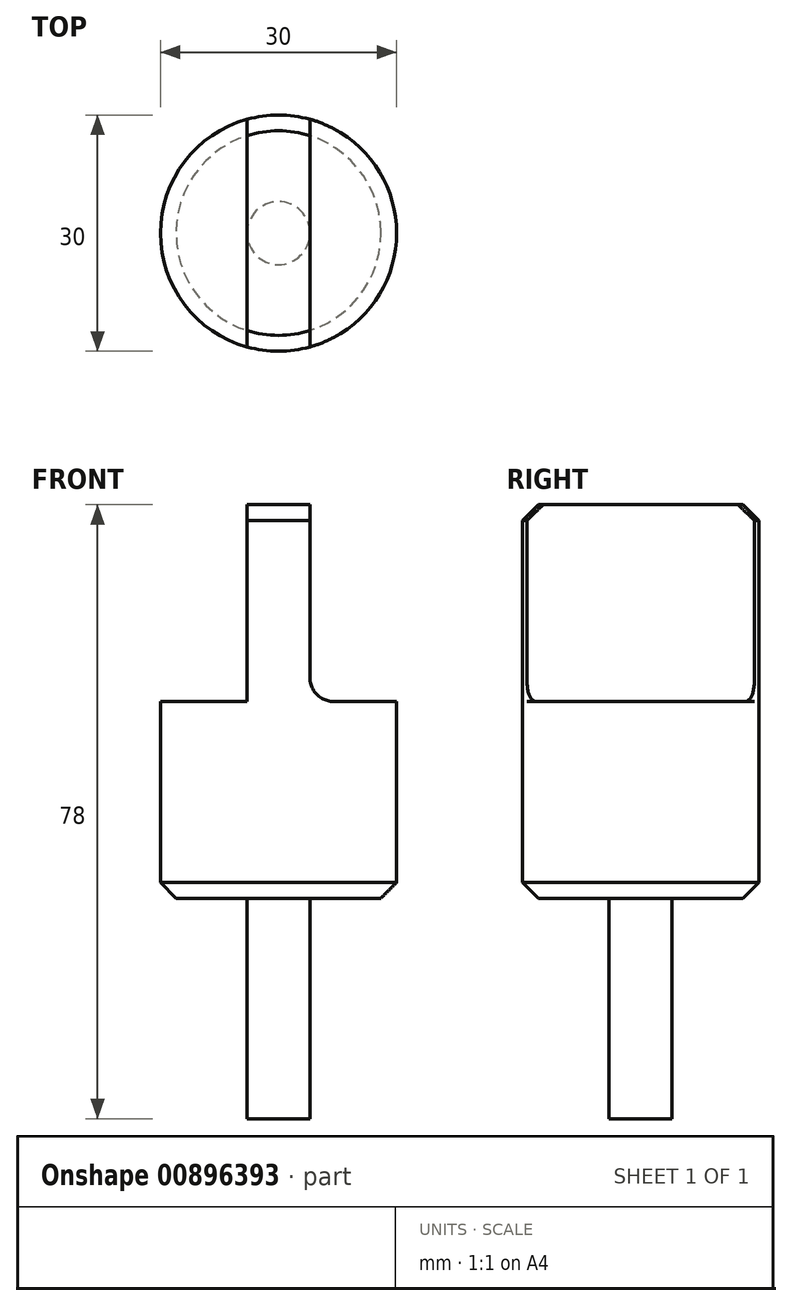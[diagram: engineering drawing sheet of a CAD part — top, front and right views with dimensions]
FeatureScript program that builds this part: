
annotation { "Feature Type Name" : "Feature", "Feature Type Description" : "" }
export const myFeature = defineFeature(function(context is Context, id is Id, definition is map)
    precondition{}
    {
        {
            var Q0;
            Q0=qCreatedBy(makeId("Top.planeOp"),FACE);
            var sketch = newSketch(context, id + "F0", { "sketchPlane" : qUnion([Q0])});
            skCircle(sketch, "E0", {"center": v(0, 0) * mm, "radius": 15 * mm});
            skCircle(sketch, "E1", {"center": v(0, 0) * mm, "radius": 4 * mm});
            skSolve(sketch);
        }
        {
            var Q0;
            Q0=makeQuery(id+"F0.imprint","IMPRINT",FACE,{"disambiguationData":[TD([[makeQuery(id+"F0.imprint","IMPRINT",EDGE,{"derivedFrom":sQuery(id+"F0.wireOp",EDGE,"E0")}),1.0]])]});
            var Q1;
            Q1=makeQuery(id+"F0.imprint","IMPRINT",FACE,{"disambiguationData":[TD([[makeQuery(id+"F0.imprint","IMPRINT",EDGE,{"derivedFrom":sQuery(id+"F0.wireOp",EDGE,"E1")}),1.0]])]});
            extrude(context, id + "F1", {"entities" : qUnion([Q0, Q1]), "depth" : 25 * mm, "offsetDistance" : 25 * mm});
        }
        {
            var Q0;
            Q0=makeQuery(id+"F0.imprint","IMPRINT",FACE,{"disambiguationData":[TD([[makeQuery(id+"F0.imprint","IMPRINT",EDGE,{"derivedFrom":sQuery(id+"F0.wireOp",EDGE,"E1")}),1.0]])]});
            extrude(context, id + "F2", {"entities" : qUnion([Q0]), "operationType" : NewBodyOperationType.ADD, "oppositeDirection" : true, "depth" : 28 * mm, "offsetDistance" : 25 * mm});
        }
        {
            var Q0;
            Q0=makeQuery(id+"F1.opExtrude","CAP_FACE",FACE,{"disambiguationData":[OSD([sQuery(id+"F0.wireOp",EDGE,"E0")])],"isStart":false});
            var sketch = newSketch(context, id + "F3", { "sketchPlane" : qUnion([Q0])});
            skLineSegment(sketch, "E2.left", {"start": v(4, 14.46) * mm, "end": v(4, -14.46) * mm});
            skLineSegment(sketch, "E2.right", {"start": v(-4, 14.46) * mm, "end": v(-4, -14.46) * mm});
            skPoint(sketch, "E2.middle", {"position": v(0, 0) * mm});
            skSolve(sketch);
        }
        {
            var Q0;
            {var subQ0=sQuery(id+"F3.wireOp",EDGE,"E2.left");Q0=makeQuery(id+"F3.imprint","IMPRINT",FACE,{"disambiguationData":[TD([[makeQuery(id+"F3.imprint","IMPRINT",EDGE,{"derivedFrom":subQ0}),-1.0]])]});}
            extrude(context, id + "F4", {"entities" : qUnion([Q0]), "operationType" : NewBodyOperationType.ADD, "depth" : 25 * mm, "offsetDistance" : 25 * mm});
        }
        {
            var Q0;
            {var subQ0=sQuery(id+"F0.wireOp",EDGE,"E0");var subQ1=makeQuery(id+"F1.opExtrude","CAP_EDGE",EDGE,{"disambiguationData":[OSD([subQ0])],"isStart":false});Q0=makeQuery(id+"F4.opExtrude","CAP_EDGE",EDGE,{"disambiguationData":[OSD([subQ0]),TDD([makeQuery(id+"F3.imprint","IMPRINT",EDGE,{"disambiguationData":[TD([[makeQuery(id+"F3.imprint","INTERSECT",VERTEX,{"disambiguationData":[OD(1.0)],"derivedFrom":[subQ1,sQuery(id+"F3.wireOp",EDGE,"E2.left")]}),1.0]])],"derivedFrom":subQ1})])],"isStart":false});}
            var Q1;
            {var subQ0=sQuery(id+"F0.wireOp",EDGE,"E0");var subQ1=makeQuery(id+"F1.opExtrude","CAP_EDGE",EDGE,{"disambiguationData":[OSD([subQ0])],"isStart":false});Q1=makeQuery(id+"F4.opExtrude","CAP_EDGE",EDGE,{"disambiguationData":[OSD([subQ0]),TDD([makeQuery(id+"F3.imprint","IMPRINT",EDGE,{"disambiguationData":[TD([[makeQuery(id+"F3.imprint","INTERSECT",VERTEX,{"disambiguationData":[OD(0.0)],"derivedFrom":[subQ1,sQuery(id+"F3.wireOp",EDGE,"E2.left")]}),-1.0]])],"derivedFrom":subQ1})])],"isStart":false});}
            chamfer(context, id + "F5", {"entities" : qUnion([Q0, Q1]), "width" : 2 * mm, "tangentPropagation" : true});
        }
        {
            var Q0;
            Q0=makeQuery(id+"F4.opExtrude","CAP_EDGE",EDGE,{"disambiguationData":[OSD([sQuery(id+"F3.wireOp",EDGE,"E2.left")])],"isStart":true});
            var Q1;
            Q1=makeQuery(id+"F4.opExtrude","CAP_EDGE",EDGE,{"disambiguationData":[OSD([sQuery(id+"F3.wireOp",EDGE,"E2.right")])],"isStart":true});
            fillet(context, id + "F6", {"entities" : qUnion([Q0, Q1]), "radius" : 3 * mm, "tangentPropagation" : true, "allowEdgeOverflow" : false});
        }
        {
            var Q0;
            Q0=makeQuery(id+"F1.opExtrude","CAP_EDGE",EDGE,{"disambiguationData":[OSD([sQuery(id+"F0.wireOp",EDGE,"E0")])],"isStart":true});
            chamfer(context, id + "F7", {"entities" : qUnion([Q0]), "width" : 2 * mm, "tangentPropagation" : true});
        }
    });
